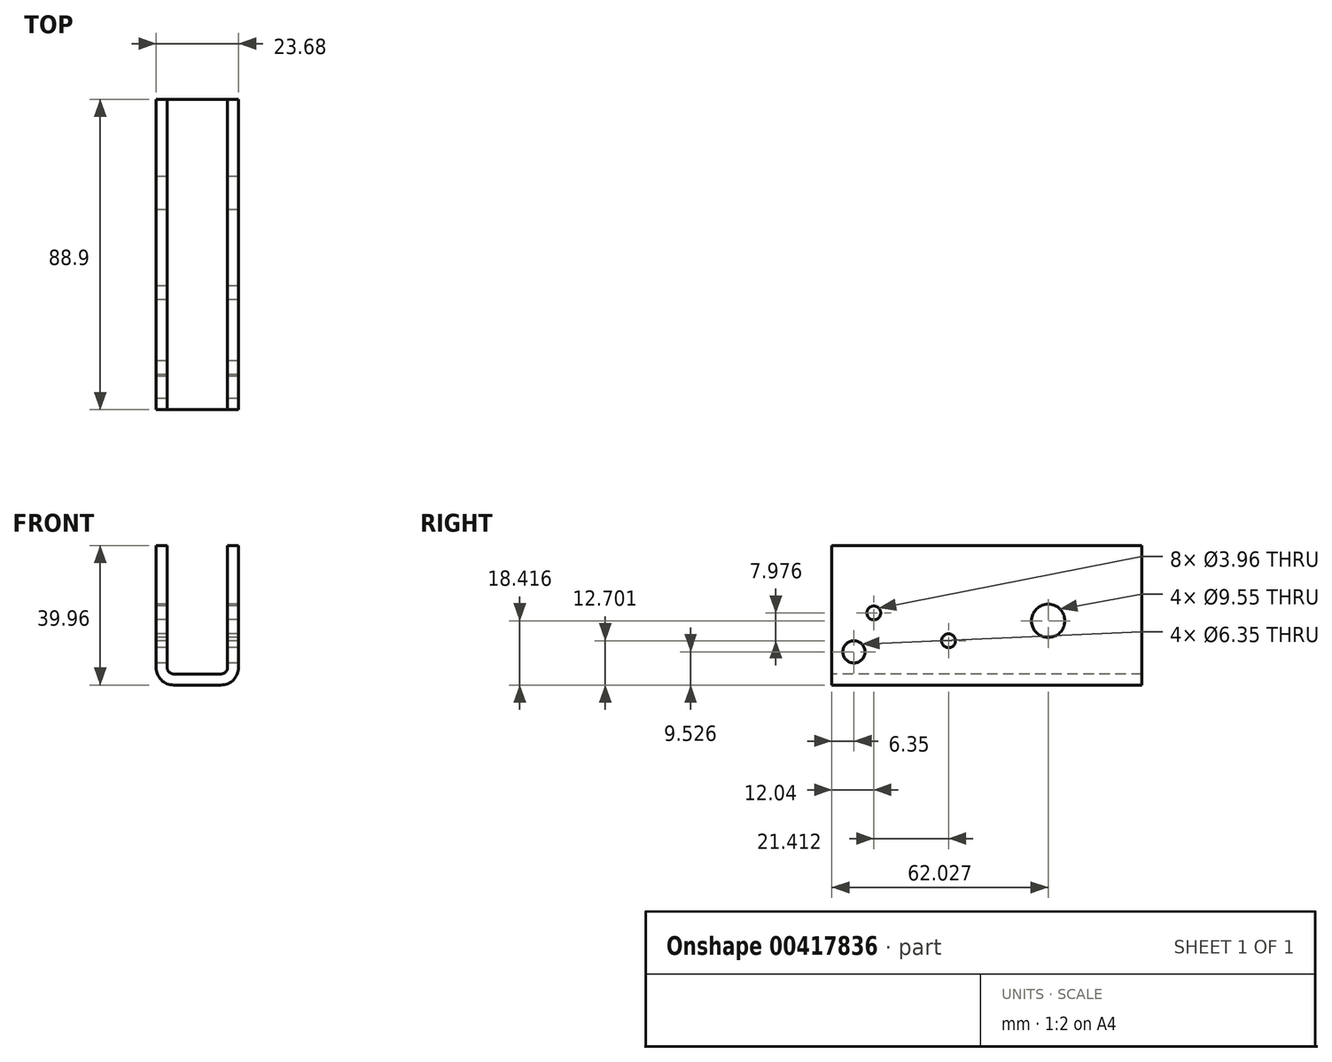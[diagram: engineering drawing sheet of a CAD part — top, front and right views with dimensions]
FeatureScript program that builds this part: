
annotation { "Feature Type Name" : "Feature", "Feature Type Description" : "" }
export const myFeature = defineFeature(function(context is Context, id is Id, definition is map)
    precondition{}
    {
        {
            var Q0;
            Q0=qCreatedBy(makeId("Right.planeOp"),FACE);
            var sketch = newSketch(context, id + "F0", { "sketchPlane" : qUnion([Q0])});
            skPoint(sketch, "E0", {"position": v(83.16, -37.7) * mm});
            skPoint(sketch, "E1", {"position": v(104.57, -45.67) * mm});
            skPoint(sketch, "E2", {"position": v(77.47, -27.2) * mm});
            skPoint(sketch, "E3", {"position": v(104.97, -55.2) * mm});
            skPoint(sketch, "E4", {"position": v(77.47, -48.84) * mm});
            skCircle(sketch, "E5", {"center": v(77.47, -48.84) * mm, "radius": 3.18 * mm});
            skPoint(sketch, "E6", {"position": v(77.47, -18.41) * mm});
            skPoint(sketch, "E7", {"position": v(133.15, -39.95) * mm});
            skCircle(sketch, "E8", {"center": v(83.16, -37.7) * mm, "radius": 1.98 * mm});
            skCircle(sketch, "E9", {"center": v(104.57, -45.67) * mm, "radius": 1.98 * mm});
            skCircle(sketch, "E10", {"center": v(133.15, -39.95) * mm, "radius": 4.78 * mm});
            skSolve(sketch);
        }
        {
            var Q0;
            Q0=qCreatedBy(makeId("Front.planeOp"),FACE);
            var sketch = newSketch(context, id + "F1", { "sketchPlane" : qUnion([Q0])});
            skLineSegment(sketch, "E11", {"start": v(-8.66, -18.41) * mm, "end": v(-8.66, -53.29) * mm});
            skLineSegment(sketch, "E12", {"start": v(-6.76, -55.2) * mm, "end": v(0, -55.2) * mm});
            skArc(sketch, "E13", {"start": v(-8.66, -53.29) * mm, "mid": v(-8.1, -54.64) * mm, "end": v(-6.76, -55.2) * mm});
            skLineSegment(sketch, "E14", {"start": v(-8.66, -18.41) * mm, "end": v(-11.84, -18.41) * mm});
            skLineSegment(sketch, "E15", {"start": v(-11.84, -18.41) * mm, "end": v(-11.84, -53.29) * mm});
            skLineSegment(sketch, "E16", {"start": v(0, -58.37) * mm, "end": v(-6.76, -58.37) * mm});
            skArc(sketch, "E17", {"start": v(-11.84, -53.29) * mm, "mid": v(-10.35, -56.88) * mm, "end": v(-6.76, -58.37) * mm});
            skLineSegment(sketch, "E18.MirrorCS", {"start": v(8.66, -18.41) * mm, "end": v(8.66, -53.29) * mm});
            skLineSegment(sketch, "E19.MirrorCS", {"start": v(11.84, -18.41) * mm, "end": v(11.84, -53.29) * mm});
            skLineSegment(sketch, "E20.MirrorCS", {"start": v(8.66, -18.41) * mm, "end": v(11.84, -18.41) * mm});
            skArc(sketch, "E21.MirrorCS", {"start": v(11.84, -53.29) * mm, "mid": v(10.35, -56.88) * mm, "end": v(6.76, -58.37) * mm});
            skArc(sketch, "E22.MirrorCS", {"start": v(8.66, -53.29) * mm, "mid": v(8.1, -54.64) * mm, "end": v(6.76, -55.2) * mm});
            skLineSegment(sketch, "E23.MirrorCS", {"start": v(6.76, -55.2) * mm, "end": v(0, -55.2) * mm});
            skLineSegment(sketch, "E24.MirrorCS", {"start": v(0, -58.37) * mm, "end": v(6.76, -58.37) * mm});
            skSolve(sketch);
        }
        {
            var Q0;
            Q0 = qSketchRegion(id + "F1", true);
            extrude(context, id + "F2", {"entities" : qUnion([Q0]), "oppositeDirection" : true, "depth" : 160.02 * mm, "hasSecondDirection" : true, "secondDirectionOppositeDirection" : true, "secondDirectionDepth" : 71.12 * mm});
        }
        {
            var Q0;
            Q0 = qSketchRegion(id + "F0", true);
            extrude(context, id + "F3", {"entities" : qUnion([Q0]), "operationType" : NewBodyOperationType.REMOVE, "depth" : 25.4 * mm, "hasSecondDirection" : true, "secondDirectionOppositeDirection" : true, "secondDirectionDepth" : 25.4 * mm});
        }
    });
